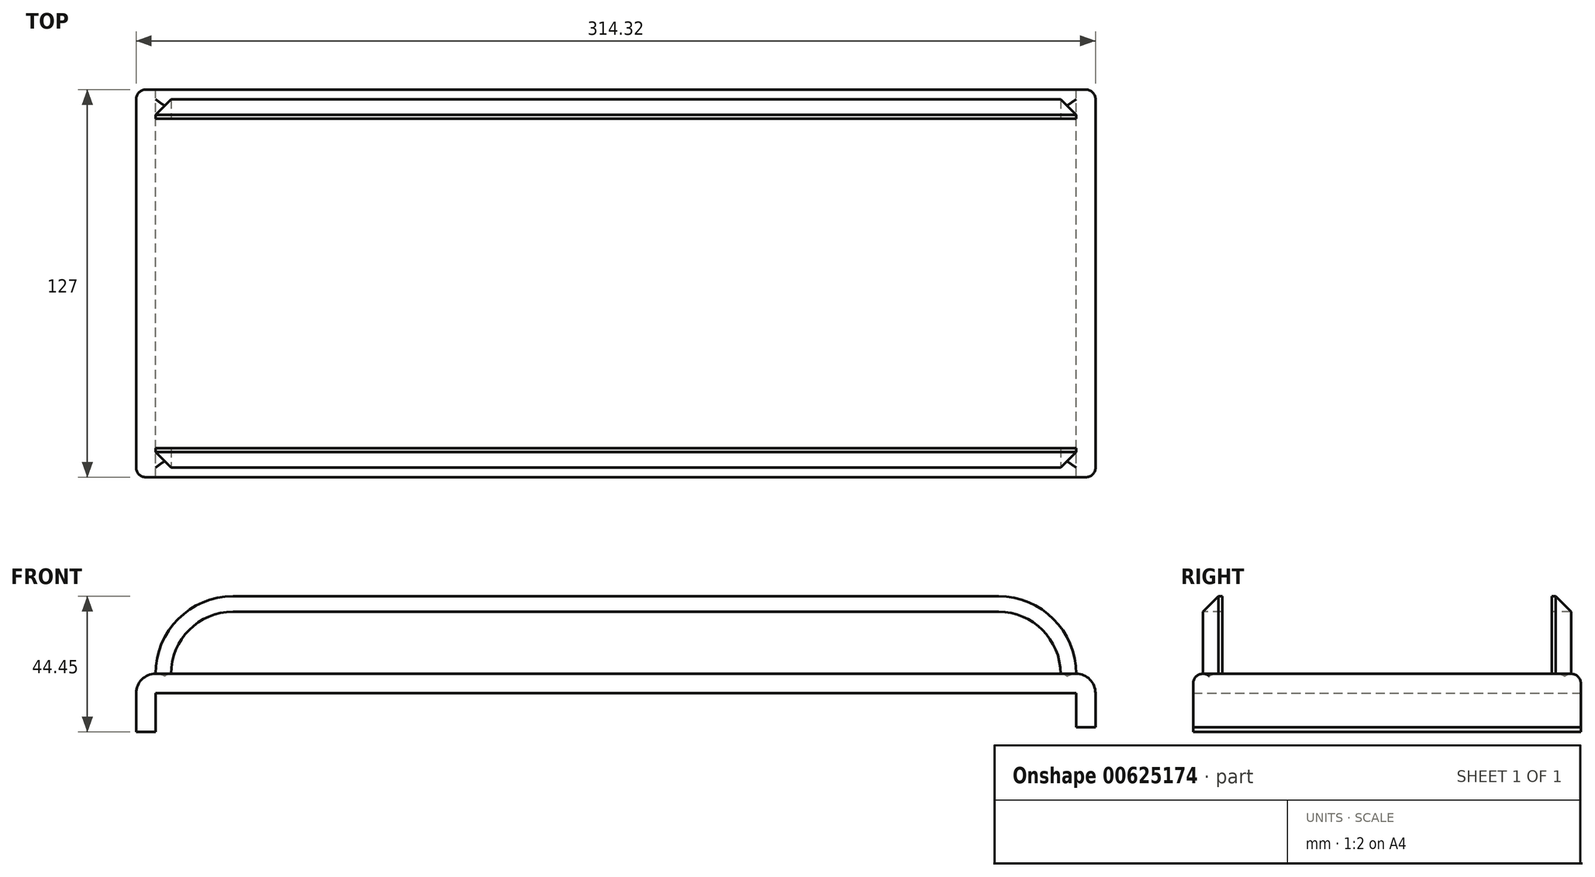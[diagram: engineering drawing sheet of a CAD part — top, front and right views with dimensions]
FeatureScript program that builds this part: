
annotation { "Feature Type Name" : "Feature", "Feature Type Description" : "" }
export const myFeature = defineFeature(function(context is Context, id is Id, definition is map)
    precondition{}
    {
        {
            var Q0;
            Q0=qCreatedBy(makeId("Front.planeOp"),FACE);
            var sketch = newSketch(context, id + "F0", { "sketchPlane" : qUnion([Q0])});
            skLineSegment(sketch, "E0.top", {"start": v(-150.81, 14.29) * mm, "end": v(150.81, 14.29) * mm});
            skLineSegment(sketch, "E0.left", {"start": v(-152.4, 0) * mm, "end": v(-152.4, 12.7) * mm});
            skLineSegment(sketch, "E0.right", {"start": v(152.4, 1.59) * mm, "end": v(152.4, 12.7) * mm});
            skPoint(sketch, "E1.visualSharp", {"position": v(-152.4, 14.29) * mm});
            skArc(sketch, "E1.filletArc", {"start": v(-150.81, 14.29) * mm, "mid": v(-151.94, 13.82) * mm, "end": v(-152.4, 12.7) * mm});
            skPoint(sketch, "E2.visualSharp", {"position": v(152.4, 14.29) * mm});
            skArc(sketch, "E2.filletArc", {"start": v(152.4, 12.7) * mm, "mid": v(151.94, 13.82) * mm, "end": v(150.81, 14.29) * mm});
            skSolve(sketch);
        }
        {
            var Q0;
            Q0=qCreatedBy(makeId("Right.planeOp"),FACE);
            var sketch = newSketch(context, id + "F1", { "sketchPlane" : qUnion([Q0])});
            skLineSegment(sketch, "E3.bottom", {"start": v(-63.5, 12.7) * mm, "end": v(63.5, 12.7) * mm});
            skLineSegment(sketch, "E3.top", {"start": v(-60.33, 19.05) * mm, "end": v(60.33, 19.05) * mm});
            skLineSegment(sketch, "E3.left", {"start": v(-63.5, 12.7) * mm, "end": v(-63.5, 15.88) * mm});
            skLineSegment(sketch, "E3.right", {"start": v(63.5, 12.7) * mm, "end": v(63.5, 15.88) * mm});
            skPoint(sketch, "E4.visualSharp", {"position": v(-63.5, 19.05) * mm});
            skArc(sketch, "E4.filletArc", {"start": v(-60.33, 19.05) * mm, "mid": v(-62.57, 18.12) * mm, "end": v(-63.5, 15.88) * mm});
            skPoint(sketch, "E5.visualSharp", {"position": v(63.5, 19.05) * mm});
            skArc(sketch, "E5.filletArc", {"start": v(63.5, 15.88) * mm, "mid": v(62.57, 18.12) * mm, "end": v(60.33, 19.05) * mm});
            skSolve(sketch);
        }
        {
            var Q0;
            Q0=makeQuery(id+"F1.imprint","IMPRINT",FACE,{"disambiguationData":[TD([[makeQuery(id+"F1.imprint","IMPRINT",EDGE,{"derivedFrom":sQuery(id+"F1.wireOp",EDGE,"E3.bottom")}),1.0]])]});
            var Q1;
            Q1 = qConstructionFilter(qBodyType(qCreatedBy(id + "F0" ,EDGE), BodyType.WIRE), ConstructionObject.NO);
            sweep(context, id + "F2", {"profiles" : qUnion([Q0]), "path" : qUnion([Q1])});
        }
        {
            var Q0;
            Q0=makeQuery(id+"F2.opSweep","SWEPT_FACE",FACE,{"disambiguationData":[OSD([sQuery(id+"F0.wireOp",EDGE,"E0.top"),sQuery(id+"F1.wireOp",EDGE,"E3.top")])]});
            var sketch = newSketch(context, id + "F3", { "sketchPlane" : qUnion([Q0])});
            skLineSegment(sketch, "E6.bottom", {"start": v(-150.81, 60.33) * mm, "end": v(150.81, 60.33) * mm});
            skLineSegment(sketch, "E6.top", {"start": v(-150.81, 53.98) * mm, "end": v(150.81, 53.98) * mm});
            skLineSegment(sketch, "E6.left", {"start": v(-150.81, 60.33) * mm, "end": v(-150.81, 53.98) * mm});
            skLineSegment(sketch, "E6.right", {"start": v(150.81, 60.33) * mm, "end": v(150.81, 53.98) * mm});
            skLineSegment(sketch, "E7.MirrorCS", {"start": v(-150.81, -53.98) * mm, "end": v(150.81, -53.98) * mm});
            skLineSegment(sketch, "E8.MirrorCS", {"start": v(-150.81, -60.33) * mm, "end": v(150.81, -60.33) * mm});
            skLineSegment(sketch, "E9.MirrorCS", {"start": v(-150.81, -60.33) * mm, "end": v(-150.81, -53.98) * mm});
            skLineSegment(sketch, "E10.MirrorCS", {"start": v(150.81, -60.33) * mm, "end": v(150.81, -53.98) * mm});
            skSolve(sketch);
        }
        {
            var Q0;
            Q0=makeQuery(id+"F3.imprint","IMPRINT",FACE,{"disambiguationData":[TD([[makeQuery(id+"F3.imprint","IMPRINT",EDGE,{"derivedFrom":sQuery(id+"F3.wireOp",EDGE,"E7.MirrorCS")}),-1.0]])]});
            var Q1;
            Q1=makeQuery(id+"F3.imprint","IMPRINT",FACE,{"disambiguationData":[TD([[makeQuery(id+"F3.imprint","IMPRINT",EDGE,{"derivedFrom":sQuery(id+"F3.wireOp",EDGE,"E6.bottom")}),-1.0]])]});
            extrude(context, id + "F4", {"entities" : qUnion([Q0, Q1]), "operationType" : NewBodyOperationType.ADD, "depth" : 25.4 * mm, "offsetDistance" : 25.4 * mm});
        }
        {
            var Q0;
            Q0=makeQuery(id+"F4.opExtrude","CAP_EDGE",EDGE,{"disambiguationData":[OSD([sQuery(id+"F3.wireOp",EDGE,"E10.MirrorCS")])],"isStart":false});
            var Q1;
            Q1=makeQuery(id+"F4.opExtrude","CAP_EDGE",EDGE,{"disambiguationData":[OSD([sQuery(id+"F3.wireOp",EDGE,"E6.right")])],"isStart":false});
            var Q2;
            Q2=makeQuery(id+"F4.opExtrude","CAP_EDGE",EDGE,{"disambiguationData":[OSD([sQuery(id+"F3.wireOp",EDGE,"E9.MirrorCS")])],"isStart":false});
            var Q3;
            Q3=makeQuery(id+"F4.opExtrude","CAP_EDGE",EDGE,{"disambiguationData":[OSD([sQuery(id+"F3.wireOp",EDGE,"E6.left")])],"isStart":false});
            fillet(context, id + "F5", {"entities" : qUnion([Q0, Q1, Q2, Q3]), "tangentPropagation" : true, "radius" : 25.4 * mm, "defaultsChanged" : true, "vertexSettings" : [], "allowEdgeOverflow" : false});
        }
        {
            var Q0;
            Q0=makeQuery(id+"F4.opExtrude","CAP_EDGE",EDGE,{"disambiguationData":[OSD([sQuery(id+"F3.wireOp",EDGE,"E6.bottom")])],"isStart":false});
            var Q1;
            Q1=makeQuery(id+"F4.opExtrude","CAP_EDGE",EDGE,{"disambiguationData":[OSD([sQuery(id+"F3.wireOp",EDGE,"E8.MirrorCS")])],"isStart":false});
            chamfer(context, id + "F6", {"entities" : qUnion([Q0, Q1]), "width" : 5.08 * mm, "tangentPropagation" : true});
        }
        {
            var Q0;
            Q0=makeQuery(id+"F4.opExtrude","SWEPT_FACE",FACE,{"disambiguationData":[OSD([sQuery(id+"F3.wireOp",EDGE,"E8.MirrorCS")])]});
            var sketch = newSketch(context, id + "F7", { "sketchPlane" : qUnion([Q0])});
            skLineSegment(sketch, "E11.bottom", {"start": v(-125.41, 39.37) * mm, "end": v(125.41, 39.37) * mm});
            skLineSegment(sketch, "E11.top", {"start": v(-125.41, 19.05) * mm, "end": v(125.41, 19.05) * mm});
            skLineSegment(sketch, "E12", {"start": v(-125.41, 19.05) * mm, "end": v(-145.73, 19.05) * mm});
            skArc(sketch, "E13", {"start": v(-145.73, 19.05) * mm, "mid": v(-139.78, 33.42) * mm, "end": v(-125.41, 39.37) * mm});
            skArc(sketch, "E14", {"start": v(145.73, 19.05) * mm, "mid": v(139.78, 33.42) * mm, "end": v(125.41, 39.37) * mm});
            skSolve(sketch);
        }
        {
            var Q0;
            Q0=makeQuery(id+"F7.imprint","IMPRINT",FACE,{"disambiguationData":[TD([[makeQuery(id+"F7.imprint","IMPRINT",EDGE,{"derivedFrom":sQuery(id+"F7.wireOp",EDGE,"E11.bottom")}),1.0]])]});
            extrude(context, id + "F8", {"entities" : qUnion([Q0]), "operationType" : NewBodyOperationType.REMOVE, "oppositeDirection" : true, "depth" : 212.1 * mm, "offsetDistance" : 25.4 * mm});
        }
    });
